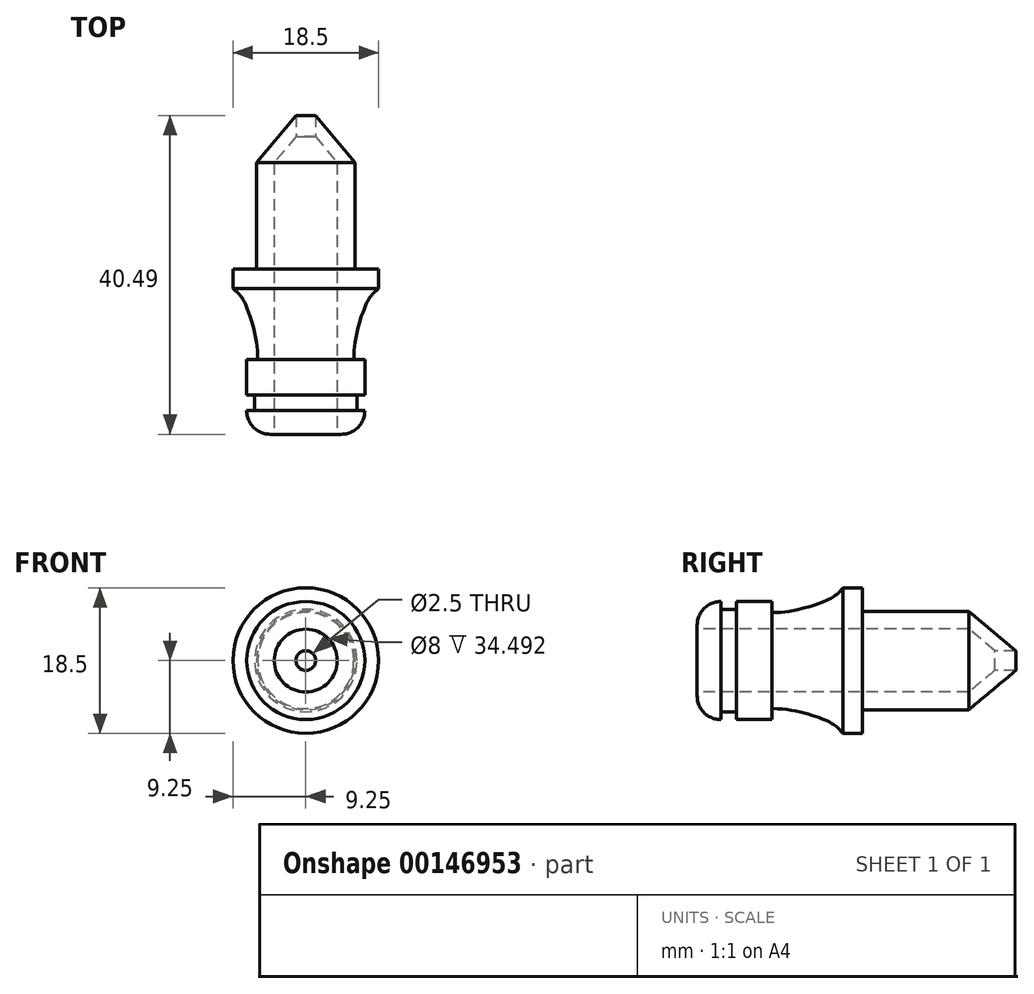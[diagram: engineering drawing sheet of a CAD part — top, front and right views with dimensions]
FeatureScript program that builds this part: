
annotation { "Feature Type Name" : "Feature", "Feature Type Description" : "" }
export const myFeature = defineFeature(function(context is Context, id is Id, definition is map)
    precondition{}
    {
        {
            var Q0;
            Q0=qCreatedBy(makeId("Top.planeOp"),FACE);
            var sketch = newSketch(context, id + "F0", { "sketchPlane" : qUnion([Q0])});
            skLineSegment(sketch, "E0", {"start": v(0, 0) * mm, "end": v(4, 0) * mm});
            skLineSegment(sketch, "E1", {"start": v(4, 0) * mm, "end": v(4, 10) * mm});
            skLineSegment(sketch, "E2", {"start": v(4, 0) * mm, "end": v(7.5, 0) * mm});
            skLineSegment(sketch, "E3", {"start": v(7.5, 0) * mm, "end": v(7.5, 3) * mm});
            skLineSegment(sketch, "E4", {"start": v(7.5, 9.5) * mm, "end": v(6.1, 9.5) * mm});
            skLineSegment(sketch, "E5", {"start": v(6.1, 9.5) * mm, "end": v(6.1, 18.5) * mm, "construction": true});
            skLineSegment(sketch, "E6", {"start": v(6.1, 9.5) * mm, "end": v(6.1, 12.5) * mm});
            skFitSpline(sketch, "E7", {"points": [v(6.1, 9.5) * mm, v(7.79, 16.75) * mm, v(9.25, 18.5) * mm], "startDerivative": vector(-0.07, 13.7) * mm, "endDerivative": vector(7, 5.93) * mm});
            skLineSegment(sketch, "E8", {"start": v(9.25, 18.5) * mm, "end": v(9.25, 21) * mm});
            skLineSegment(sketch, "E9", {"start": v(9.25, 21) * mm, "end": v(6.25, 21) * mm});
            skLineSegment(sketch, "E10", {"start": v(6.25, 21) * mm, "end": v(6.25, 24) * mm});
            skLineSegment(sketch, "E11", {"start": v(4, 10) * mm, "end": v(4, 24) * mm});
            skLineSegment(sketch, "E12", {"start": v(4, 24) * mm, "end": v(6.25, 24) * mm});
            skLineSegment(sketch, "E13", {"start": v(0, 0) * mm, "end": v(0, 28.67) * mm, "construction": true});
            skLineSegment(sketch, "E14", {"start": v(6.25, 24) * mm, "end": v(6.25, 34.5) * mm});
            skLineSegment(sketch, "E15", {"start": v(6.25, 34.5) * mm, "end": v(4, 34.5) * mm});
            skLineSegment(sketch, "E16", {"start": v(4, 34.5) * mm, "end": v(4, 24) * mm});
            skLineSegment(sketch, "E17", {"start": v(6.25, 34.5) * mm, "end": v(6.25, 40.5) * mm, "construction": true});
            skLineSegment(sketch, "E18", {"start": v(6.25, 40.5) * mm, "end": v(1.25, 40.5) * mm, "construction": true});
            skLineSegment(sketch, "E19", {"start": v(6.25, 34.5) * mm, "end": v(1.25, 40.5) * mm});
            skLineSegment(sketch, "E20", {"start": v(4, 34.5) * mm, "end": v(1.25, 37.8) * mm});
            skLineSegment(sketch, "E21", {"start": v(1.25, 37.8) * mm, "end": v(1.25, 40.5) * mm});
            skLineSegment(sketch, "E22", {"start": v(9.25, 18.5) * mm, "end": v(6.1, 18.5) * mm, "construction": true});
            skLineSegment(sketch, "E23", {"start": v(7.5, 3) * mm, "end": v(6.5, 3) * mm});
            skLineSegment(sketch, "E24", {"start": v(6.5, 3) * mm, "end": v(6.5, 5) * mm});
            skLineSegment(sketch, "E25", {"start": v(6.5, 5) * mm, "end": v(7.5, 5) * mm});
            skLineSegment(sketch, "E26.trimOffspring", {"start": v(7.5, 5) * mm, "end": v(7.5, 9.5) * mm});
            skSolve(sketch);
        }
        {
            var Q0;
            Q0 = qSketchRegion(id + "F0", true);
            var Q1;
            Q1=sQuery(id+"F0.wireOp",EDGE,"E13");
            revolve(context, id + "F1", {"entities" : qUnion([Q0]), "axis" : qUnion([Q1]), "revolveType" : RevolveType.FULL});
        }
        {
            var Q0;
            Q0=makeQuery(id+"F1.opRevolve","SWEPT_EDGE",EDGE,{"disambiguationData":[OSD([sQuery(id+"F0.wireOp",EDGE,"E2"),sQuery(id+"F0.wireOp",EDGE,"E3")])]});
            fillet(context, id + "F2", {"entities" : qUnion([Q0]), "radius" : 3 * mm, "tangentPropagation" : true, "allowEdgeOverflow" : false});
        }
    });
